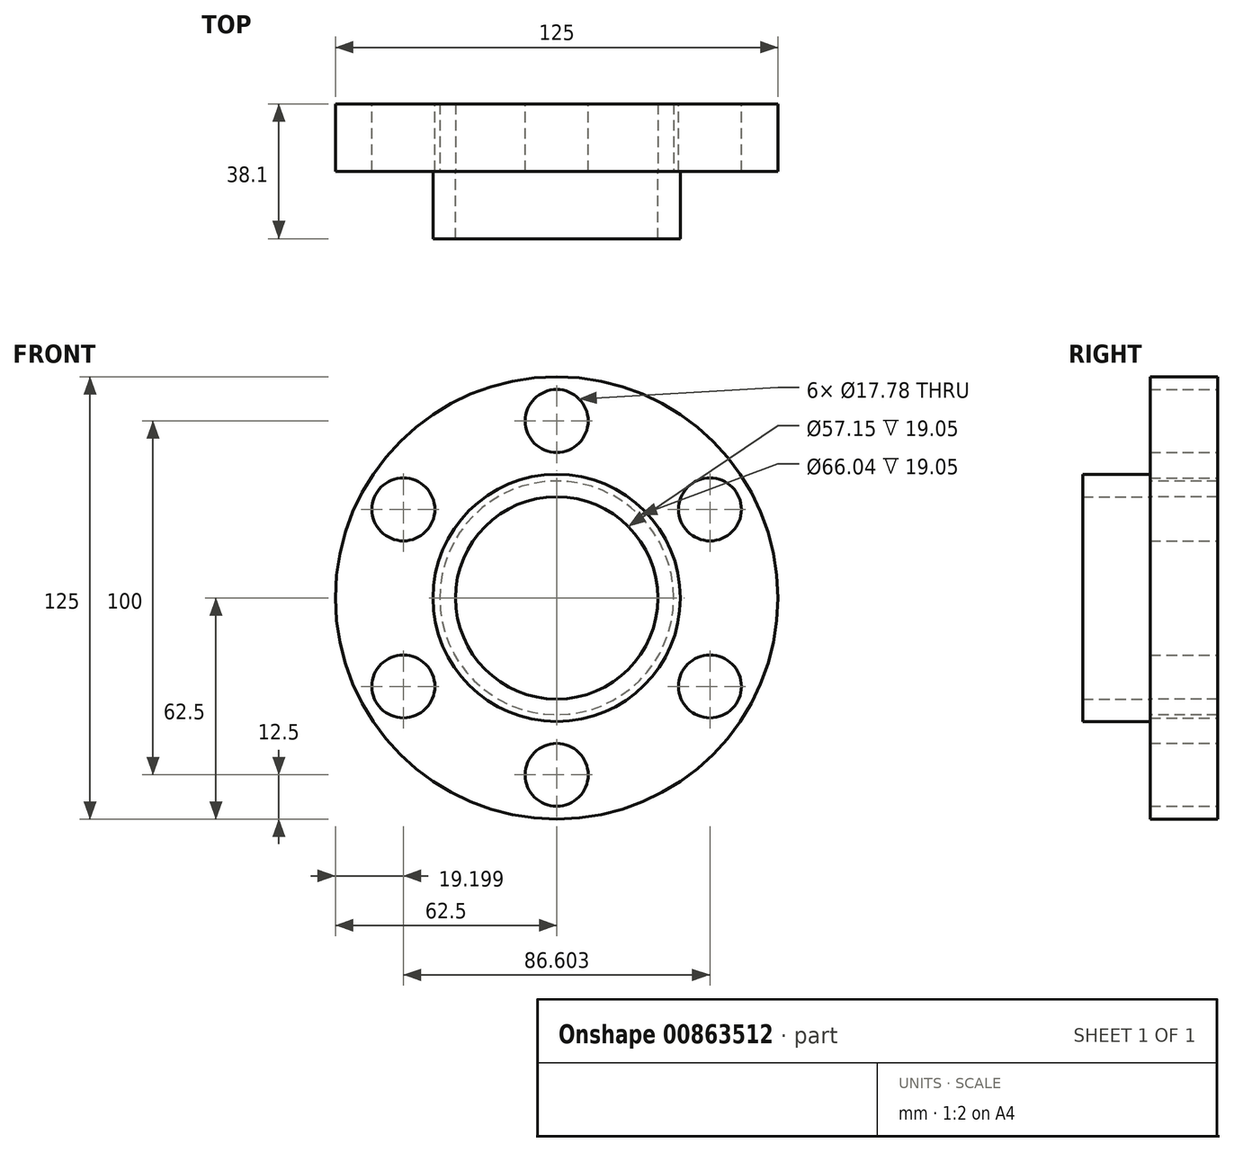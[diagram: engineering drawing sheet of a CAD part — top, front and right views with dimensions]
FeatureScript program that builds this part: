
annotation { "Feature Type Name" : "Feature", "Feature Type Description" : "" }
export const myFeature = defineFeature(function(context is Context, id is Id, definition is map)
    precondition{}
    {
        {
            var Q0;
            Q0=qCreatedBy(makeId("Front.planeOp"),FACE);
            var sketch = newSketch(context, id + "F0", { "sketchPlane" : qUnion([Q0])});
            skCircle(sketch, "E0", {"center": v(0, 0) * mm, "radius": 62.5 * mm});
            skCircle(sketch, "E1", {"center": v(0, 0) * mm, "radius": 50 * mm, "construction": true});
            skLineSegment(sketch, "E2", {"start": v(0, 0) * mm, "end": v(0, 87.92) * mm});
            skCircle(sketch, "E3", {"center": v(0, 50) * mm, "radius": 8.9 * mm});
            skCircle(sketch, "E4.1.0", {"center": v(-43.3, 25) * mm, "radius": 8.9 * mm});
            skCircle(sketch, "E4.2.0", {"center": v(-43.3, -25) * mm, "radius": 8.9 * mm});
            skCircle(sketch, "E4.3.0", {"center": v(0, -50) * mm, "radius": 8.9 * mm});
            skCircle(sketch, "E4.4.0", {"center": v(43.3, -25) * mm, "radius": 8.9 * mm});
            skCircle(sketch, "E4.5.0", {"center": v(43.3, 25) * mm, "radius": 8.9 * mm});
            skSolve(sketch);
        }
        {
            var Q0;
            Q0=makeQuery(id+"F0.imprint","IMPRINT",FACE,{"disambiguationData":[TD([[makeQuery(id+"F0.imprint","IMPRINT",EDGE,{"derivedFrom":sQuery(id+"F0.wireOp",EDGE,"E0")}),1.0]])]});
            extrude(context, id + "F1", {"entities" : qUnion([Q0]), "depth" : 19.05 * mm});
        }
        {
            var Q0;
            Q0=makeQuery(id+"F1.opExtrude","CAP_FACE",FACE,{"disambiguationData":[OSD([sQuery(id+"F0.wireOp",EDGE,"E0"),sQuery(id+"F0.wireOp",EDGE,"47804e7a-2431-4f3c-b785-4ff43a304412"),sQuery(id+"F0.wireOp",EDGE,"d4718459-af55-4dad-8911-bd223aa27aa5.1.0"),sQuery(id+"F0.wireOp",EDGE,"d4718459-af55-4dad-8911-bd223aa27aa5.2.0"),sQuery(id+"F0.wireOp",EDGE,"d4718459-af55-4dad-8911-bd223aa27aa5.3.0"),sQuery(id+"F0.wireOp",EDGE,"d4718459-af55-4dad-8911-bd223aa27aa5.4.0"),sQuery(id+"F0.wireOp",EDGE,"d4718459-af55-4dad-8911-bd223aa27aa5.5.0")])],"isStart":false});
            var sketch = newSketch(context, id + "F2", { "sketchPlane" : qUnion([Q0])});
            skCircle(sketch, "E5", {"center": v(0, 0) * mm, "radius": 34.93 * mm});
            skCircle(sketch, "E6", {"center": v(0, 0) * mm, "radius": 28.58 * mm});
            skSolve(sketch);
        }
        {
            var Q0;
            Q0=makeQuery(id+"F2.imprint","IMPRINT",FACE,{"disambiguationData":[TD([[makeQuery(id+"F2.imprint","IMPRINT",EDGE,{"derivedFrom":sQuery(id+"F2.wireOp",EDGE,"E5")}),1.0]])]});
            extrude(context, id + "F3", {"entities" : qUnion([Q0]), "operationType" : NewBodyOperationType.ADD, "depth" : 19.05 * mm});
        }
        {
            var Q0;
            Q0=makeQuery(id+"F3.boolean.opBoolean","SPLIT",FACE,{"disambiguationData":[TD([makeQuery(id+"F3.opExtrude","SWEPT_FACE",FACE,{"disambiguationData":[OSD([sQuery(id+"F2.wireOp",EDGE,"E6")])]})])],"derivedFrom":makeQuery(id+"F1.opExtrude","CAP_FACE",FACE,{"disambiguationData":[OSD([sQuery(id+"F0.wireOp",EDGE,"E0"),sQuery(id+"F0.wireOp",EDGE,"47804e7a-2431-4f3c-b785-4ff43a304412"),sQuery(id+"F0.wireOp",EDGE,"d4718459-af55-4dad-8911-bd223aa27aa5.1.0"),sQuery(id+"F0.wireOp",EDGE,"d4718459-af55-4dad-8911-bd223aa27aa5.2.0"),sQuery(id+"F0.wireOp",EDGE,"d4718459-af55-4dad-8911-bd223aa27aa5.3.0"),sQuery(id+"F0.wireOp",EDGE,"d4718459-af55-4dad-8911-bd223aa27aa5.4.0"),sQuery(id+"F0.wireOp",EDGE,"d4718459-af55-4dad-8911-bd223aa27aa5.5.0")])],"isStart":false})});
            var sketch = newSketch(context, id + "F4", { "sketchPlane" : qUnion([Q0])});
            skCircle(sketch, "E7", {"center": v(0, 0) * mm, "radius": 33.02 * mm});
            skSolve(sketch);
        }
        {
            var Q0;
            Q0=makeQuery(id+"F4.imprint","IMPRINT",FACE,{"disambiguationData":[TD([[makeQuery(id+"F4.imprint","IMPRINT",EDGE,{"derivedFrom":sQuery(id+"F4.wireOp",EDGE,"E7")}),1.0]])]});
            extrude(context, id + "F5", {"entities" : qUnion([Q0]), "operationType" : NewBodyOperationType.REMOVE, "oppositeDirection" : true, "depth" : 25.4 * mm});
        }
    });
